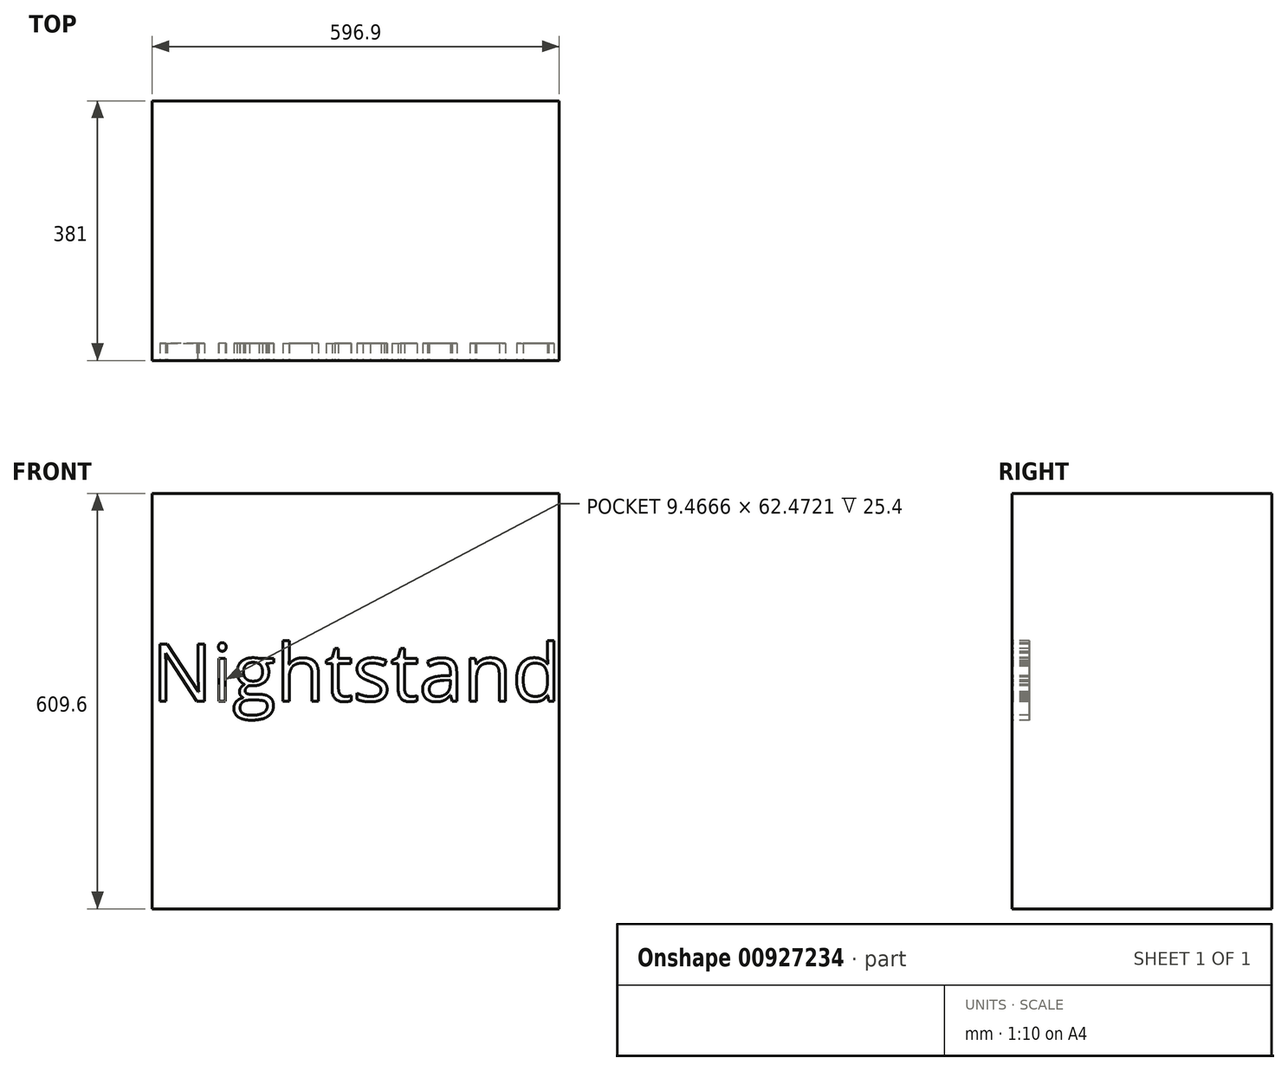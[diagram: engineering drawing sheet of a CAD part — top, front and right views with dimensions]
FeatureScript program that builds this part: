
annotation { "Feature Type Name" : "Feature", "Feature Type Description" : "" }
export const myFeature = defineFeature(function(context is Context, id is Id, definition is map)
    precondition{}
    {
        {
            var Q0;
            Q0=qCreatedBy(makeId("Front.planeOp"),FACE);
            var sketch = newSketch(context, id + "F0", { "sketchPlane" : qUnion([Q0])});
            skLineSegment(sketch, "E0.bottom", {"start": v(298.45, -304.8) * mm, "end": v(-298.45, -304.8) * mm});
            skLineSegment(sketch, "E0.top", {"start": v(298.45, 304.8) * mm, "end": v(-298.45, 304.8) * mm});
            skLineSegment(sketch, "E0.left", {"start": v(298.45, -304.8) * mm, "end": v(298.45, 304.8) * mm});
            skLineSegment(sketch, "E0.right", {"start": v(-298.45, -304.8) * mm, "end": v(-298.45, 304.8) * mm});
            skPoint(sketch, "E0.middle", {"position": v(0, 0) * mm});
            skSolve(sketch);
        }
        {
            var Q0;
            Q0 = qSketchRegion(id + "F0", true);
            extrude(context, id + "F1", {"entities" : qUnion([Q0]), "endBound" : BoundingType.SYMMETRIC, "depth" : 381 * mm, "offsetDistance" : 25.4 * mm});
        }
        {
            var Q0;
            Q0=makeQuery(id+"F1.opExtrude","CAP_FACE",FACE,{"disambiguationData":[OSD([sQuery(id+"F0.wireOp",EDGE,"E0.bottom"),sQuery(id+"F0.wireOp",EDGE,"E0.top"),sQuery(id+"F0.wireOp",EDGE,"E0.left"),sQuery(id+"F0.wireOp",EDGE,"E0.right")])],"isStart":false});
            var sketch = newSketch(context, id + "F2", { "sketchPlane" : qUnion([Q0])});
            skText(sketch, "E1", { "text": "Nightstand", "fontName": "OpenSans-Regular.ttf"});
            const initialGuessF2  = {"E1": [-0.29845, 0, 1, 0, 0.08405]};
            skSetInitialGuess(sketch, initialGuessF2);
            skSolve(sketch);
        }
        {
            var Q0;
            Q0 = qSketchRegion(id + "F2", true);
            extrude(context, id + "F3", {"entities" : qUnion([Q0]), "operationType" : NewBodyOperationType.REMOVE, "oppositeDirection" : true, "depth" : 25.4 * mm, "offsetDistance" : 25.4 * mm});
        }
    });
